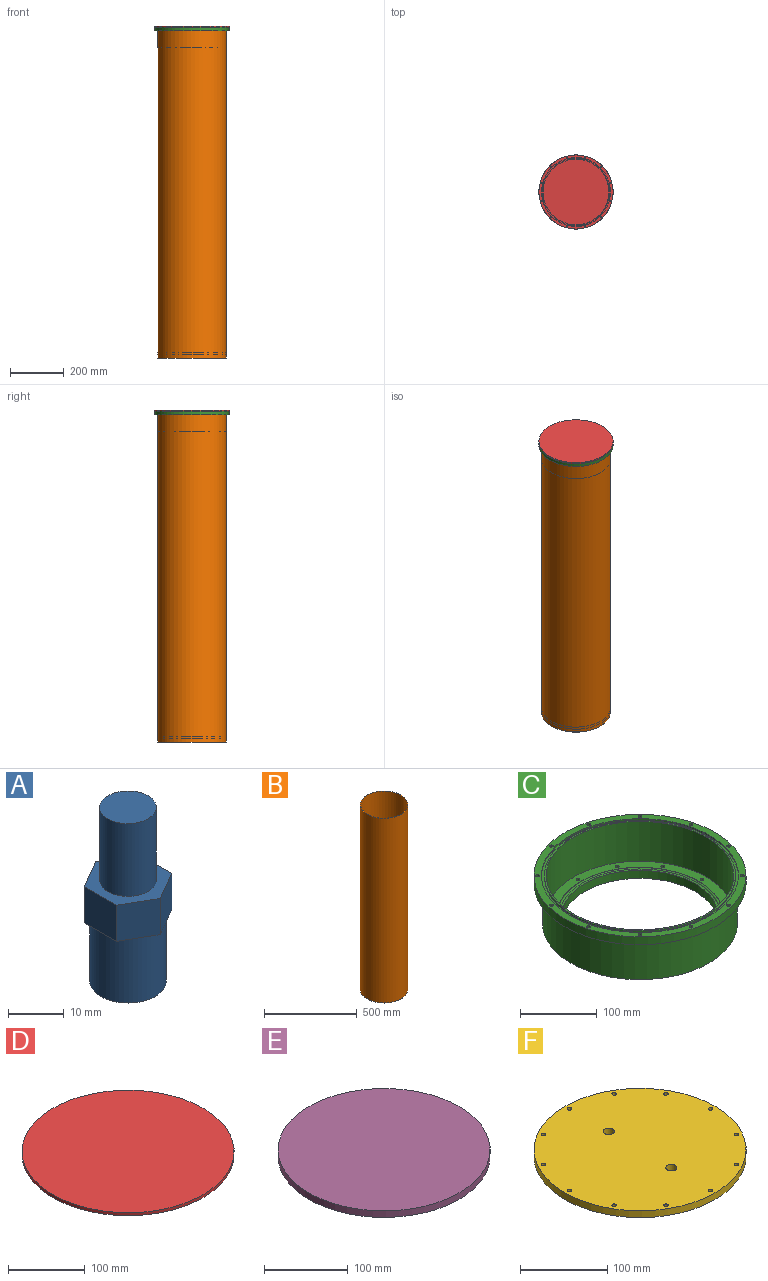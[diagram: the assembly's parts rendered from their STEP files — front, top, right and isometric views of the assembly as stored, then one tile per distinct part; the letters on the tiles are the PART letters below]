
ASSEMBLY  parts=6 mates=5
PART A: 12 faces, bbox 14.1x16.3x38.1 mm
  f0: plane 16.26x14.08mm, normal (0,0,-1), area 23.9mm2, adj f2,f6,f7,f8,f9,f10,f11
  f1: plane 13.72x13.72mm, normal (0,0,-1), area 147.8mm2, adj f2
  f2: cylinder r=6.86mm len=14.22mm, axis (0,0,1), area 612.9mm2, adj f0,f1
  f3: plane 16.26x14.08mm, normal (0,0,1), area 90.6mm2, adj f4,f6,f7,f8,f9,f10,f11
  f4: cylinder r=5.08mm len=15.95mm, axis (0,0,1), area 509.1mm2, adj f3,f5
  f5: plane 10.16x10.16mm, normal (0,0,1), area 81.1mm2, adj f4
  f6: plane 7.92x7.04mm, normal (-0.5,0.87,0), area 64.4mm2, adj f0,f3,f9,f11
  f7: plane 8.13x7.92mm, normal (1,0,0), area 64.4mm2, adj f0,f3,f9,f10
  f8: plane 7.92x7.04mm, normal (-0.5,-0.87,0), area 64.4mm2, adj f0,f3,f10,f11
  f9: plane 7.92x7.04mm, normal (0.5,0.87,0), area 64.4mm2, adj f0,f3,f6,f7
  f10: plane 7.92x7.04mm, normal (0.5,-0.87,0), area 64.4mm2, adj f0,f3,f7,f8
  f11: plane 8.13x7.92mm, normal (-1,0,0), area 64.4mm2, adj f0,f3,f6,f8
PART B: 4 faces, bbox 256x256x1219.2 mm
  f0: cylinder r=127mm len=1219.2mm, axis (0,0,-1), area 972878.4mm2, adj f2,f3
  f1: cylinder r=127.99mm len=1219.2mm, axis (0,0,-1), area 980466.8mm2, adj f2,f3
  f2: plane 255.98x255.98mm, normal (0,0,1), area 793.5mm2, adj f0,f1
  f3: plane 255.98x255.98mm, normal (0,0,-1), area 793.5mm2, adj f0,f1
PART C: 54 faces, bbox 276.2x276.2x76.2 mm
  f0: plane 217.17x217.17mm, normal (0,0,1), area 546mm2, adj f1,f17
  f1: torus R=106.68mm, axis (0,0,-1), area 5053.6mm2, adj f0,f2
  f2: plane 211.16x211.16mm, normal (0,0,1), area 530.9mm2, adj f1,f3
  f3: cylinder r=104.77mm len=209.55mm, axis (0,0,-1), area 1504.9mm2, adj f2,f4
  f4: plane 209.55x209.55mm, normal (0,0,1), area 2058.5mm2, adj f3,f5
  f5: cylinder r=101.6mm len=203.2mm, axis (0,0,-1), area 8107.3mm2, adj f4,f6
  f6: plane 254x254mm, normal (0,0,-1), area 18241.5mm2, adj f5,f7
  f7: cylinder r=127mm len=254mm, axis (0,0,-1), area 50670.7mm2, adj f6,f8
  f8: plane 276.23x276.23mm, normal (0,0,-1), area 9041.6mm2, adj f7,f9,f42,f43,f44,f45,f46,f47
  f9: cylinder r=138.11mm len=276.23mm, axis (0,0,-1), area 11020.9mm2, adj f8,f10
  f10: plane 276.23x276.23mm, normal (0,0,1), area 7971.9mm2, adj f9,f11,f42,f43,f44,f45,f46,f47
  f11: cylinder r=128.33mm len=256.67mm, axis (0,0,-1), area 1843.3mm2, adj f10,f12
  f12: plane 256.67x256.67mm, normal (0,0,1), area 3026.6mm2, adj f11,f13
  f13: cylinder r=124.52mm len=249.05mm, axis (0,0,-1), area 1788.6mm2, adj f12,f14
  f14: plane 249.05x249.05mm, normal (0,0,1), area 1772.2mm2, adj f13,f15
  f15: cylinder r=122.24mm len=244.48mm, axis (0,0,-1), area 48770.6mm2, adj f14,f16
  f16: plane 244.48x244.48mm, normal (0,0,1), area 9697mm2, adj f15,f17,f18,f20,f22,f24,f26,f28
  f17: cylinder r=108.59mm len=217.17mm, axis (0,0,-1), area 1559.6mm2, adj f0,f16
  f18: cylinder r=2.32mm len=9.53mm, axis (0,0,1), area 138.9mm2, adj f16,f19
  f19: plane 4.64x4.64mm, normal (0,0,1), area 16.9mm2, adj f18
  f20: cylinder r=2.32mm len=9.53mm, axis (0,0,1), area 138.9mm2, adj f16,f21
  f21: plane 4.64x4.64mm, normal (0,0,1), area 16.9mm2, adj f20
  f22: cylinder r=2.32mm len=9.53mm, axis (0,0,1), area 138.9mm2, adj f16,f23
  f23: plane 4.64x4.64mm, normal (0,0,1), area 16.9mm2, adj f22
  f24: cylinder r=2.32mm len=9.53mm, axis (0,0,1), area 138.9mm2, adj f16,f25
  f25: plane 4.64x4.64mm, normal (0,0,1), area 16.9mm2, adj f24
  f26: cylinder r=2.32mm len=9.53mm, axis (0,0,1), area 138.9mm2, adj f16,f27
  f27: plane 4.64x4.64mm, normal (0,0,1), area 16.9mm2, adj f26
  f28: cylinder r=2.32mm len=9.53mm, axis (0,0,1), area 138.9mm2, adj f16,f29
  f29: plane 4.64x4.64mm, normal (0,0,1), area 16.9mm2, adj f28
  f30: cylinder r=2.32mm len=9.53mm, axis (0,0,1), area 138.9mm2, adj f16,f31
  f31: plane 4.64x4.64mm, normal (0,0,1), area 16.9mm2, adj f30
  f32: cylinder r=2.32mm len=9.53mm, axis (0,0,1), area 138.9mm2, adj f16,f33
  f33: plane 4.64x4.64mm, normal (0,0,1), area 16.9mm2, adj f32
  f34: cylinder r=2.32mm len=9.53mm, axis (0,0,1), area 138.9mm2, adj f16,f35
  f35: plane 4.64x4.64mm, normal (0,0,1), area 16.9mm2, adj f34
  f36: cylinder r=2.32mm len=9.53mm, axis (0,0,1), area 138.9mm2, adj f16,f37
  f37: plane 4.64x4.64mm, normal (0,0,1), area 16.9mm2, adj f36
  f38: cylinder r=2.32mm len=9.53mm, axis (0,0,1), area 138.9mm2, adj f16,f39
  f39: plane 4.64x4.64mm, normal (0,0,1), area 16.9mm2, adj f38
  f40: cylinder r=2.32mm len=9.53mm, axis (0,0,1), area 138.9mm2, adj f16,f41
  f41: plane 4.64x4.64mm, normal (0,0,1), area 16.9mm2, adj f40
  f42: cylinder r=2.38mm len=12.7mm, axis (0,0,1), area 190mm2, adj f8,f10
  f43: cylinder r=2.38mm len=12.7mm, axis (0,0,1), area 190mm2, adj f8,f10
  f44: cylinder r=2.38mm len=12.7mm, axis (0,0,1), area 190mm2, adj f8,f10
  f45: cylinder r=2.38mm len=12.7mm, axis (0,0,1), area 190mm2, adj f8,f10
  f46: cylinder r=2.38mm len=12.7mm, axis (0,0,1), area 190mm2, adj f8,f10
  f47: cylinder r=2.38mm len=12.7mm, axis (0,0,1), area 190mm2, adj f8,f10
  f48: cylinder r=2.38mm len=12.7mm, axis (0,0,1), area 190mm2, adj f8,f10
  f49: cylinder r=2.38mm len=12.7mm, axis (0,0,1), area 190mm2, adj f8,f10
  f50: cylinder r=2.38mm len=12.7mm, axis (0,0,1), area 190mm2, adj f8,f10
  f51: cylinder r=2.38mm len=12.7mm, axis (0,0,1), area 190mm2, adj f8,f10
  f52: cylinder r=2.38mm len=12.7mm, axis (0,0,1), area 190mm2, adj f8,f10
  f53: cylinder r=2.38mm len=12.7mm, axis (0,0,1), area 190mm2, adj f8,f10
PART D: 3 faces, bbox 276.2x276.2x4.8 mm
  f0: cylinder r=138.11mm len=276.23mm, axis (0,0,-1), area 4132.8mm2, adj f1,f2
  f1: plane 276.23x276.23mm, normal (0,0,1), area 59926.1mm2, adj f0
  f2: plane 276.23x276.23mm, normal (0,0,-1), area 59926.1mm2, adj f0
PART E: 3 faces, bbox 254x254x9.5 mm
  f0: cylinder r=127mm len=254mm, axis (0,0,-1), area 7600.6mm2, adj f1,f2
  f1: plane 254x254mm, normal (0,0,1), area 50670.7mm2, adj f0
  f2: plane 254x254mm, normal (0,0,-1), area 50670.7mm2, adj f0
PART F: 17 faces, bbox 242.9x242.9x9.5 mm
  f0: cylinder r=121.44mm len=242.89mm, axis (0,0,-1), area 7268.1mm2, adj f1,f2
  f1: plane 242.89x242.89mm, normal (0,0,1), area 45837.5mm2, adj f0,f3,f4,f5,f6,f7,f8,f9
  f2: plane 242.89x242.89mm, normal (0,0,-1), area 45837.5mm2, adj f0,f3,f4,f5,f6,f7,f8,f9
  f3: cylinder r=2.54mm len=9.53mm, axis (0,0,1), area 152mm2, adj f1,f2
  f4: cylinder r=2.54mm len=9.53mm, axis (0,0,1), area 152mm2, adj f1,f2
  f5: cylinder r=2.54mm len=9.53mm, axis (0,0,1), area 152mm2, adj f1,f2
  f6: cylinder r=2.54mm len=9.53mm, axis (0,0,1), area 152mm2, adj f1,f2
  f7: cylinder r=2.54mm len=9.53mm, axis (0,0,1), area 152mm2, adj f1,f2
  f8: cylinder r=2.54mm len=9.53mm, axis (0,0,1), area 152mm2, adj f1,f2
  f9: cylinder r=2.54mm len=9.53mm, axis (0,0,1), area 152mm2, adj f1,f2
  f10: cylinder r=2.54mm len=9.53mm, axis (0,0,1), area 152mm2, adj f1,f2
  f11: cylinder r=2.54mm len=9.53mm, axis (0,0,1), area 152mm2, adj f1,f2
  f12: cylinder r=2.54mm len=9.53mm, axis (0,0,1), area 152mm2, adj f1,f2
  f13: cylinder r=2.54mm len=9.53mm, axis (0,0,1), area 152mm2, adj f1,f2
  f14: cylinder r=2.54mm len=9.53mm, axis (0,0,1), area 152mm2, adj f1,f2
  f15: cylinder r=6.35mm len=12.7mm, axis (0,0,1), area 380mm2, adj f1,f2
  f16: cylinder r=6.35mm len=12.7mm, axis (0,0,1), area 380mm2, adj f1,f2
PLACE A t=(-807.55,113.22,919.34)mm
PLACE B t=(-807.55,164.02,-248.42)mm
PLACE C t=(-807.55,164.02,907.28)mm
PLACE D t=(-807.55,164.02,983.48)mm
PLACE E t=(-807.55,164.02,-235.72)mm
PLACE F t=(-807.55,164.02,919.98)mm
MATE fastened B.f1 <-> C.f1  axis (0,0,1) through (-807.55,164.02,970.78)mm
MATE fastened F.f0 <-> C.f1  axis (0,0,-1) through (-807.55,164.02,919.98)mm
MATE fastened A.f2 <-> F.f16  axis (0,0,-1) through (-807.55,113.22,919.34)mm
MATE fastened E.f0 <-> B.f0  axis (0,0,-1) through (-807.55,164.02,-235.72)mm
MATE fastened D.f0 <-> C.f1  axis (0,0,-1) through (-807.55,164.02,983.48)mm
